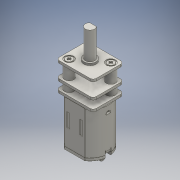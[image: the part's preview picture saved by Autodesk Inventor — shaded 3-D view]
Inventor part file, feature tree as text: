
AUTODESK INVENTOR PART (.ipt)
format: ipt  version: 2016 (Build 200138000, 138)  size: 587,776 bytes
history: native  units: mm
features: other x1, fillet x1
ambient origin geometry x8: Origin, YZ Plane, XZ Plane, XY Plane, X Axis, Y Axis, Z Axis, Center Point
bodies: Body1 (feature_tree)
feature tree (2):
  other  "Sólido1"
  fillet  "Redondeo14"  [1 undecoded]
note: 1 required parameter value undecoded (feature->parameter linkage not recoverable at this tier; creation-order binding heuristic only, values carry confidence <= 0.55)
